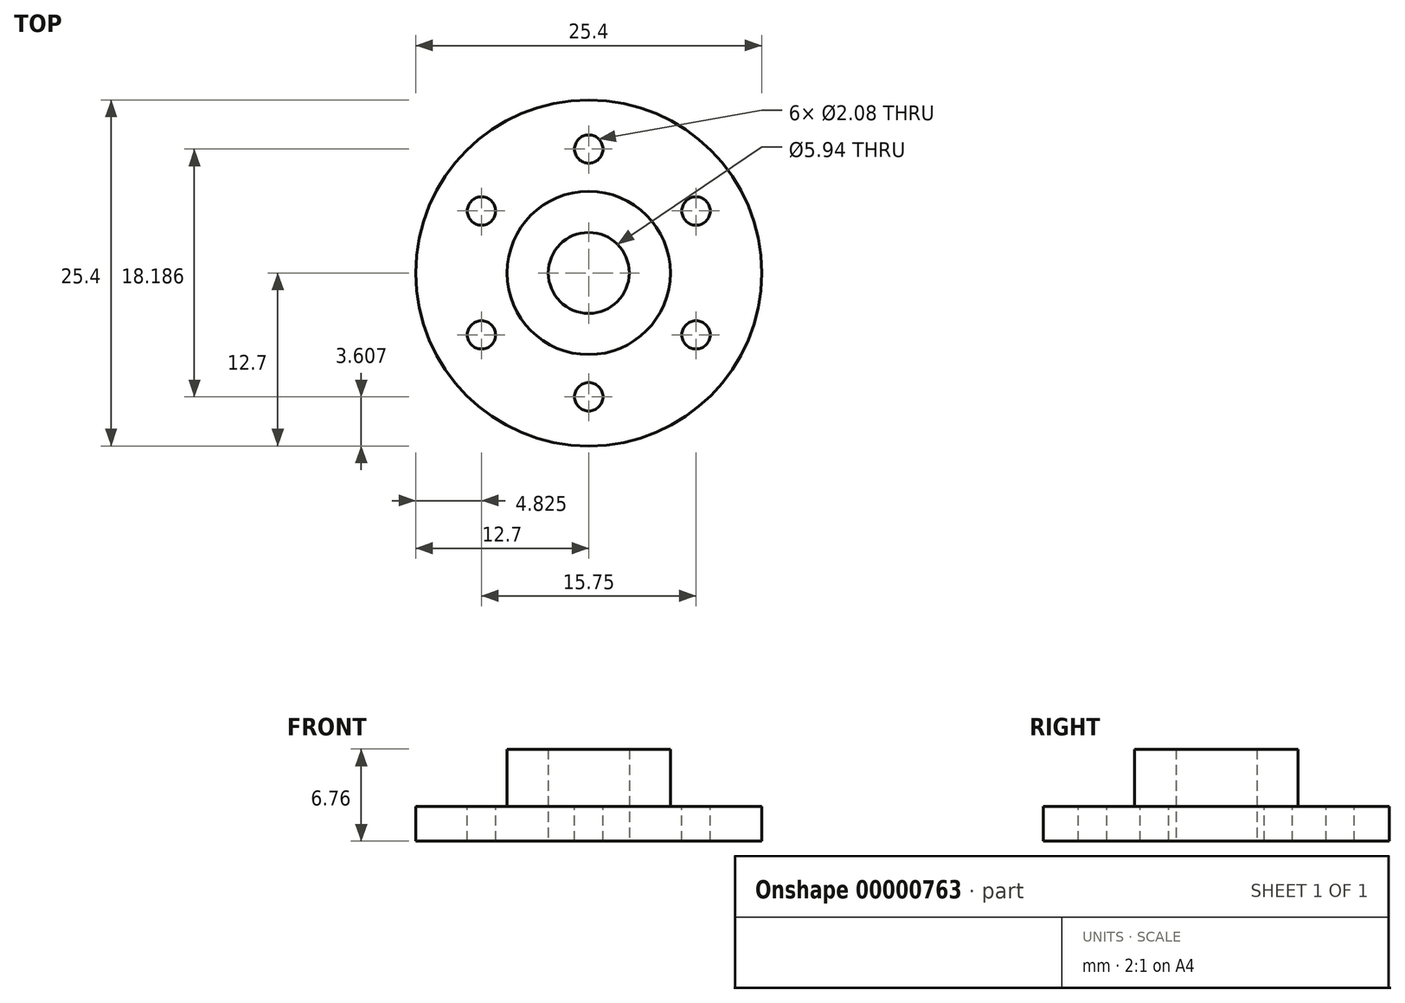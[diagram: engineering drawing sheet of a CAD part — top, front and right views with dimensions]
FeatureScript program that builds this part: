
annotation { "Feature Type Name" : "Feature", "Feature Type Description" : "" }
export const myFeature = defineFeature(function(context is Context, id is Id, definition is map)
    precondition{}
    {
        {
            var Q0;
            Q0=qCreatedBy(makeId("Top.planeOp"),FACE);
            var sketch = newSketch(context, id + "F0", { "sketchPlane" : qUnion([Q0])});
            skCircle(sketch, "E0", {"center": v(0, 0) * mm, "radius": 12.7 * mm});
            skSolve(sketch);
        }
        {
            var Q0;
            Q0=makeQuery(id+"F0.imprint","IMPRINT",FACE,{"disambiguationData":[TD([[makeQuery(id+"F0.imprint","IMPRINT",EDGE,{"derivedFrom":sQuery(id+"F0.wireOp",EDGE,"E0")}),1.0]])]});
            extrude(context, id + "F1", {"entities" : qUnion([Q0]), "depth" : 2.54 * mm});
        }
        {
            var Q0;
            Q0=makeQuery(id+"F1.opExtrude","CAP_FACE",FACE,{"disambiguationData":[OSD([sQuery(id+"F0.wireOp",EDGE,"E0")])],"isStart":false});
            var sketch = newSketch(context, id + "F2", { "sketchPlane" : qUnion([Q0])});
            skCircle(sketch, "E1", {"center": v(0, 0) * mm, "radius": 6 * mm});
            skCircle(sketch, "E2", {"center": v(0, 0) * mm, "radius": 2.97 * mm});
            skSolve(sketch);
        }
        {
            var Q0;
            Q0=makeQuery(id+"F2.imprint","IMPRINT",FACE,{"disambiguationData":[TD([[makeQuery(id+"F2.imprint","IMPRINT",EDGE,{"derivedFrom":sQuery(id+"F2.wireOp",EDGE,"E1")}),1.0]])]});
            extrude(context, id + "F3", {"entities" : qUnion([Q0]), "operationType" : NewBodyOperationType.ADD, "depth" : 4.22 * mm});
        }
        {
            var Q0;
            {var subQ0=sQuery(id+"F0.wireOp",EDGE,"E0");Q0=makeQuery(id+"F3.boolean.opBoolean","SPLIT",FACE,{"disambiguationData":[TD([makeQuery(id+"F1.opExtrude","SWEPT_FACE",FACE,{"disambiguationData":[OSD([subQ0])]})])],"derivedFrom":makeQuery(id+"F1.opExtrude","CAP_FACE",FACE,{"disambiguationData":[OSD([subQ0])],"isStart":false})});}
            var sketch = newSketch(context, id + "F4", { "sketchPlane" : qUnion([Q0])});
            skCircle(sketch, "E3", {"center": v(0, -9.1) * mm, "radius": 1.04 * mm});
            skLineSegment(sketch, "E4", {"start": v(0, -6) * mm, "end": v(0, -8.05) * mm, "construction": true});
            skSolve(sketch);
        }
        {
            var Q0;
            Q0=makeQuery(id+"F4.imprint","IMPRINT",FACE,{"disambiguationData":[TD([[makeQuery(id+"F4.imprint","IMPRINT",EDGE,{"derivedFrom":sQuery(id+"F4.wireOp",EDGE,"E3")}),1.0]])]});
            extrude(context, id + "F5", {"entities" : qUnion([Q0]), "operationType" : NewBodyOperationType.REMOVE, "endBound" : BoundingType.THROUGH_ALL, "oppositeDirection" : true, "depth" : 25.4 * mm});
        }
        {
            var Q0;
            Q0=makeQuery(id+"F5.boolean.opBoolean","COPY",FACE,{"derivedFrom":makeQuery(id+"F5.opExtrude","SWEPT_FACE",FACE,{"disambiguationData":[OSD([sQuery(id+"F4.wireOp",EDGE,"E3")])]})});
            var Q1;
            Q1=makeQuery(id+"F3.opExtrude","CAP_EDGE",EDGE,{"disambiguationData":[OSD([sQuery(id+"F2.wireOp",EDGE,"E1")])],"isStart":false});
            circularPattern(context, id + "F6", {"faces" : qUnion([Q0]), "axis" : qUnion([Q1]), "angle" : 360 * degree, "instanceCount" : 6, "equalSpace" : true, "patternType" : PatternType.FACE});
        }
        {
            var Q0;
            Q0=makeQuery(id+"F3.boolean.opBoolean","SPLIT",FACE,{"disambiguationData":[TD([makeQuery(id+"F3.opExtrude","SWEPT_FACE",FACE,{"disambiguationData":[OSD([sQuery(id+"F2.wireOp",EDGE,"E2")])]})])],"derivedFrom":makeQuery(id+"F1.opExtrude","CAP_FACE",FACE,{"disambiguationData":[OSD([sQuery(id+"F0.wireOp",EDGE,"E0")])],"isStart":false})});
            extrude(context, id + "F7", {"entities" : qUnion([Q0]), "operationType" : NewBodyOperationType.REMOVE, "endBound" : BoundingType.THROUGH_ALL, "oppositeDirection" : true, "depth" : 25.4 * mm});
        }
    });
